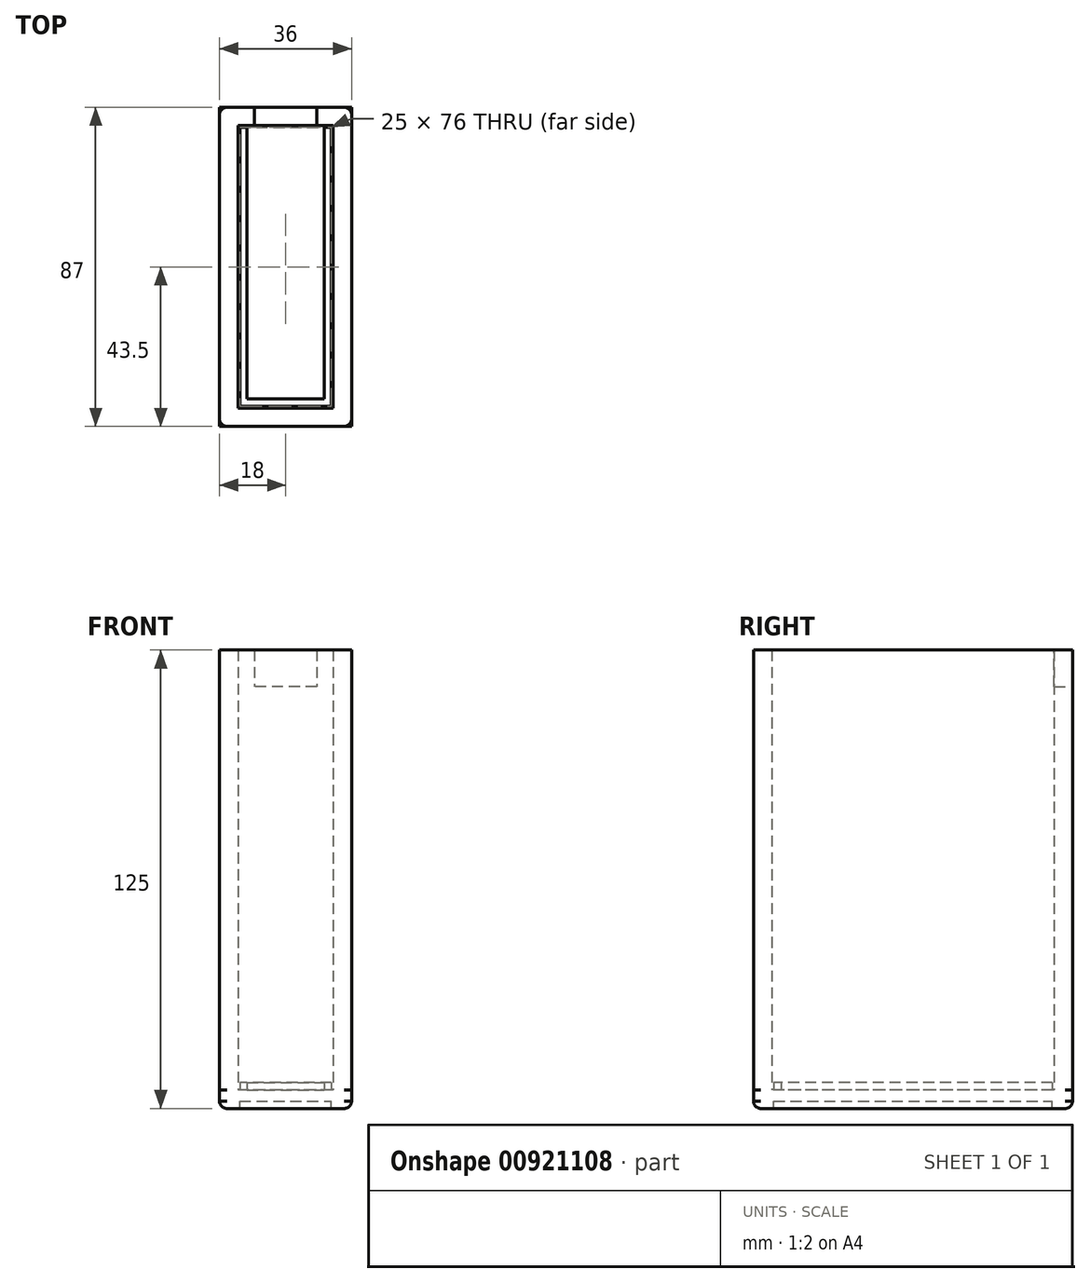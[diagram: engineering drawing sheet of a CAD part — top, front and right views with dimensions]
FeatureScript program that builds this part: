
annotation { "Feature Type Name" : "Feature", "Feature Type Description" : "" }
export const myFeature = defineFeature(function(context is Context, id is Id, definition is map)
    precondition{}
    {
        {
            var Q0;
            Q0=qCreatedBy(makeId("Top.planeOp"),FACE);
            var sketch = newSketch(context, id + "F0", { "sketchPlane" : qUnion([Q0])});
            skLineSegment(sketch, "E0.bottom", {"start": v(13, 38.5) * mm, "end": v(-13, 38.5) * mm});
            skLineSegment(sketch, "E0.top", {"start": v(13, -38.5) * mm, "end": v(-13, -38.5) * mm});
            skLineSegment(sketch, "E0.left", {"start": v(13, 38.5) * mm, "end": v(13, -38.5) * mm});
            skLineSegment(sketch, "E0.right", {"start": v(-13, 38.5) * mm, "end": v(-13, -38.5) * mm});
            skPoint(sketch, "E0.middle", {"position": v(0, 0) * mm});
            skLineSegment(sketch, "E1.0", {"start": v(-18, 43.5) * mm, "end": v(-18, -43.5) * mm});
            skLineSegment(sketch, "E1.1", {"start": v(18, 43.5) * mm, "end": v(-18, 43.5) * mm});
            skLineSegment(sketch, "E1.2", {"start": v(18, 43.5) * mm, "end": v(18, -43.5) * mm});
            skLineSegment(sketch, "E1.3", {"start": v(18, -43.5) * mm, "end": v(-18, -43.5) * mm});
            skLineSegment(sketch, "E2.0", {"start": v(12.5, -38) * mm, "end": v(-12.5, -38) * mm});
            skLineSegment(sketch, "E2.1", {"start": v(12.5, 38) * mm, "end": v(12.5, -38) * mm});
            skLineSegment(sketch, "E2.2", {"start": v(12.5, 38) * mm, "end": v(-12.5, 38) * mm});
            skLineSegment(sketch, "E2.3", {"start": v(-12.5, 38) * mm, "end": v(-12.5, -38) * mm});
            skLineSegment(sketch, "E3", {"start": v(-10.5, 38) * mm, "end": v(-10.5, -36) * mm});
            skLineSegment(sketch, "E4", {"start": v(-10.5, -36) * mm, "end": v(10.5, -36) * mm});
            skLineSegment(sketch, "E5", {"start": v(10.5, -36) * mm, "end": v(10.5, 38) * mm});
            skSolve(sketch);
        }
        {
            var Q0;
            Q0=makeQuery(id+"F0.imprint","IMPRINT",FACE,{"disambiguationData":[TD([[makeQuery(id+"F0.imprint","IMPRINT",EDGE,{"derivedFrom":sQuery(id+"F0.wireOp",EDGE,"E0.bottom")}),-1.0]])]});
            extrude(context, id + "F1", {"entities" : qUnion([Q0]), "depth" : 120 * mm, "offsetDistance" : 25 * mm});
        }
        {
            var Q0;
            Q0=makeQuery(id+"F0.imprint","IMPRINT",FACE,{"disambiguationData":[TD([[makeQuery(id+"F0.imprint","IMPRINT",EDGE,{"derivedFrom":sQuery(id+"F0.wireOp",EDGE,"E0.bottom")}),1.0]])]});
            var Q1;
            Q1=makeQuery(id+"F0.imprint","IMPRINT",FACE,{"disambiguationData":[TD([[makeQuery(id+"F0.imprint","IMPRINT",EDGE,{"derivedFrom":sQuery(id+"F0.wireOp",EDGE,"E0.bottom")}),-1.0]])]});
            extrude(context, id + "F2", {"entities" : qUnion([Q0, Q1]), "operationType" : NewBodyOperationType.ADD, "oppositeDirection" : true, "depth" : 5 * mm, "offsetDistance" : 25 * mm});
        }
        {
            var Q0;
            Q0=makeQuery(id+"F2.opExtrude","CAP_EDGE",EDGE,{"disambiguationData":[OSD([sQuery(id+"F0.wireOp",EDGE,"E1.1")])],"isStart":false});
            var Q1;
            Q1=makeQuery(id+"F2.opExtrude","CAP_EDGE",EDGE,{"disambiguationData":[OSD([sQuery(id+"F0.wireOp",EDGE,"E1.3")])],"isStart":false});
            var Q2;
            {var subQ0=sQuery(id+"F0.wireOp",EDGE,"E1.3");var subQ1=sQuery(id+"F0.wireOp",EDGE,"E1.0");Q2=makeQuery(id+"F2.boolean.opBoolean","MERGE",EDGE,{"derivedFrom":[makeQuery(id+"F1.opExtrude","SWEPT_EDGE",EDGE,{"disambiguationData":[OSD([subQ1,subQ0])]}),makeQuery(id+"F2.opExtrude","SWEPT_EDGE",EDGE,{"disambiguationData":[OSD([subQ1,subQ0])]})]});}
            var Q3;
            Q3=makeQuery(id+"F2.opExtrude","CAP_EDGE",EDGE,{"disambiguationData":[OSD([sQuery(id+"F0.wireOp",EDGE,"E1.2")])],"isStart":false});
            var Q4;
            {var subQ0=sQuery(id+"F0.wireOp",EDGE,"E1.3");var subQ1=sQuery(id+"F0.wireOp",EDGE,"E1.2");Q4=makeQuery(id+"F2.boolean.opBoolean","MERGE",EDGE,{"derivedFrom":[makeQuery(id+"F1.opExtrude","SWEPT_EDGE",EDGE,{"disambiguationData":[OSD([subQ1,subQ0])]}),makeQuery(id+"F2.opExtrude","SWEPT_EDGE",EDGE,{"disambiguationData":[OSD([subQ1,subQ0])]})]});}
            var Q5;
            {var subQ0=sQuery(id+"F0.wireOp",EDGE,"E1.2");var subQ1=sQuery(id+"F0.wireOp",EDGE,"E1.1");Q5=makeQuery(id+"F2.boolean.opBoolean","MERGE",EDGE,{"derivedFrom":[makeQuery(id+"F1.opExtrude","SWEPT_EDGE",EDGE,{"disambiguationData":[OSD([subQ1,subQ0])]}),makeQuery(id+"F2.opExtrude","SWEPT_EDGE",EDGE,{"disambiguationData":[OSD([subQ1,subQ0])]})]});}
            var Q6;
            Q6=makeQuery(id+"F2.opExtrude","CAP_EDGE",EDGE,{"disambiguationData":[OSD([sQuery(id+"F0.wireOp",EDGE,"E1.0")])],"isStart":false});
            var Q7;
            {var subQ0=sQuery(id+"F0.wireOp",EDGE,"E1.1");var subQ1=sQuery(id+"F0.wireOp",EDGE,"E1.0");Q7=makeQuery(id+"F2.boolean.opBoolean","MERGE",EDGE,{"derivedFrom":[makeQuery(id+"F1.opExtrude","SWEPT_EDGE",EDGE,{"disambiguationData":[OSD([subQ1,subQ0])]}),makeQuery(id+"F2.opExtrude","SWEPT_EDGE",EDGE,{"disambiguationData":[OSD([subQ1,subQ0])]})]});}
            fillet(context, id + "F3", {"entities" : qUnion([Q0, Q1, Q2, Q3, Q4, Q5, Q6, Q7]), "radius" : 2 * mm, "tangentPropagation" : true, "allowEdgeOverflow" : false});
        }
        {
            var Q0;
            {var subQ0=sQuery(id+"F0.wireOp",EDGE,"E1.1");Q0=makeQuery(id+"F2.boolean.opBoolean","MERGE",FACE,{"derivedFrom":[makeQuery(id+"F1.opExtrude","SWEPT_FACE",FACE,{"disambiguationData":[OSD([subQ0])]}),makeQuery(id+"F2.opExtrude","SWEPT_FACE",FACE,{"disambiguationData":[OSD([subQ0])]})]});}
            var sketch = newSketch(context, id + "F4", { "sketchPlane" : qUnion([Q0])});
            skLineSegment(sketch, "E6.bottom", {"start": v(-8.5, 120) * mm, "end": v(8.5, 120) * mm});
            skLineSegment(sketch, "E6.top", {"start": v(-8.5, 110) * mm, "end": v(8.5, 110) * mm});
            skLineSegment(sketch, "E6.left", {"start": v(-8.5, 120) * mm, "end": v(-8.5, 110) * mm});
            skLineSegment(sketch, "E6.right", {"start": v(8.5, 120) * mm, "end": v(8.5, 110) * mm});
            skLineSegment(sketch, "E7", {"start": v(0, 120) * mm, "end": v(0, 95.1) * mm, "construction": true});
            skPoint(sketch, "E8", {"position": v(0, 120) * mm});
            skSolve(sketch);
        }
        {
            var Q0;
            Q0=makeQuery(id+"F4.imprint","IMPRINT",FACE,{"disambiguationData":[TD([[makeQuery(id+"F4.imprint","IMPRINT",EDGE,{"derivedFrom":sQuery(id+"F4.wireOp",EDGE,"E6.bottom")}),-1.0]])]});
            var sketch = newSketch(context, id + "F5", { "sketchPlane" : qUnion([Q0])});
            skSolve(sketch);
        }
        {
            var Q0;
            Q0=makeQuery(id+"F5.imprint","IMPRINT",FACE,{"disambiguationData":[TD([[makeQuery(id+"F5.imprint","IMPRINT",EDGE,{"derivedFrom":makeQuery(id+"F4.imprint","IMPRINT",EDGE,{"derivedFrom":sQuery(id+"F4.wireOp",EDGE,"E6.bottom")})}),-1.0]])]});
            extrude(context, id + "F6", {"entities" : qUnion([Q0]), "operationType" : NewBodyOperationType.REMOVE, "oppositeDirection" : true, "depth" : 25 * mm, "offsetDistance" : 25 * mm});
        }
        {
            var Q0;
            Q0=makeQuery(id+"F0.imprint","IMPRINT",FACE,{"disambiguationData":[TD([[makeQuery(id+"F0.imprint","IMPRINT",EDGE,{"derivedFrom":sQuery(id+"F0.wireOp",EDGE,"E2.0")}),-1.0]])]});
            extrude(context, id + "F7", {"entities" : qUnion([Q0]), "depth" : 2 * mm, "offsetDistance" : 25 * mm});
        }
        {
            var Q0;
            Q0=makeQuery(id+"F0.imprint","IMPRINT",FACE,{"disambiguationData":[TD([[makeQuery(id+"F0.imprint","IMPRINT",EDGE,{"derivedFrom":sQuery(id+"F0.wireOp",EDGE,"E2.0")}),-1.0]])]});
            var Q1;
            {var subQ0=sQuery(id+"F0.wireOp",EDGE,"E3");Q1=makeQuery(id+"F0.imprint","IMPRINT",FACE,{"disambiguationData":[TD([[makeQuery(id+"F0.imprint","IMPRINT",EDGE,{"derivedFrom":subQ0}),1.0]])]});}
            var Q2;
            Q2=makeQuery(id+"F0.imprint","IMPRINT",FACE,{"disambiguationData":[TD([[makeQuery(id+"F0.imprint","IMPRINT",EDGE,{"derivedFrom":sQuery(id+"F0.wireOp",EDGE,"E0.bottom")}),-1.0]])]});
            var Q3;
            Q3=makeQuery(id+"F0.imprint","IMPRINT",FACE,{"disambiguationData":[TD([[makeQuery(id+"F0.imprint","IMPRINT",EDGE,{"derivedFrom":sQuery(id+"F0.wireOp",EDGE,"E0.bottom")}),1.0]])]});
            extrude(context, id + "F8", {"entities" : qUnion([Q0, Q1, Q2, Q3]), "operationType" : NewBodyOperationType.ADD, "oppositeDirection" : true, "depth" : 3 * mm, "offsetDistance" : 25 * mm});
        }
    });
